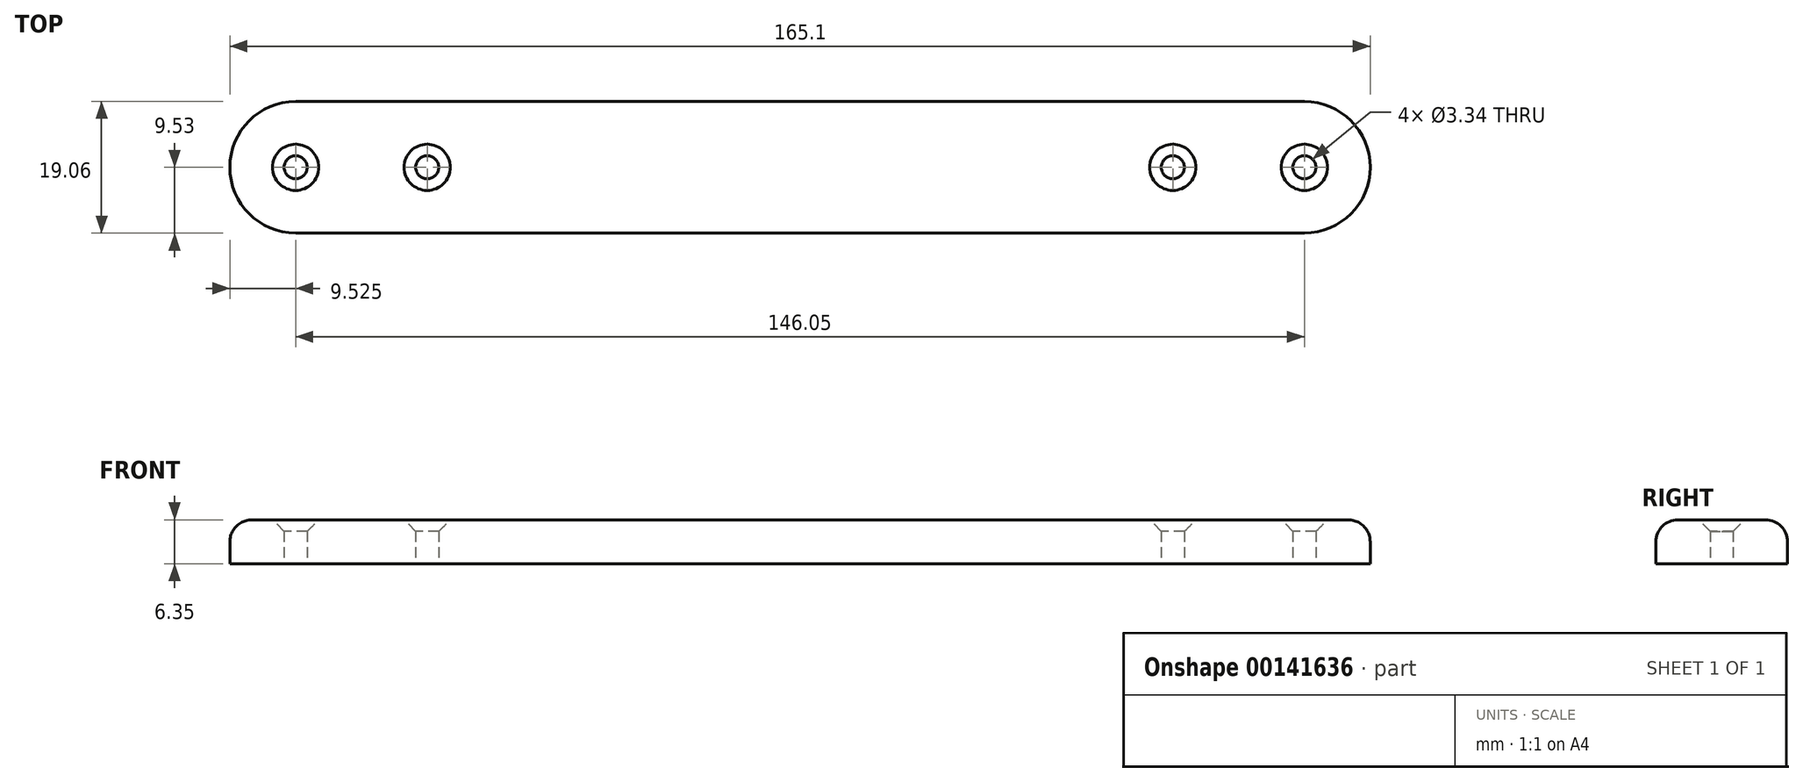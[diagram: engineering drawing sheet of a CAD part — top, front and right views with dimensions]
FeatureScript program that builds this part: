
annotation { "Feature Type Name" : "Feature", "Feature Type Description" : "" }
export const myFeature = defineFeature(function(context is Context, id is Id, definition is map)
    precondition{}
    {
        {
            var Q0;
            Q0=qCreatedBy(makeId("Top.planeOp"),FACE);
            var sketch = newSketch(context, id + "F0", { "sketchPlane" : qUnion([Q0])});
            skLineSegment(sketch, "E0.bottom", {"start": v(63.5, 9.53) * mm, "end": v(-63.5, 9.53) * mm});
            skLineSegment(sketch, "E0.top", {"start": v(63.5, -9.53) * mm, "end": v(-63.5, -9.53) * mm});
            skLineSegment(sketch, "E0.left", {"start": v(63.5, 9.53) * mm, "end": v(63.5, -9.53) * mm, "construction": true});
            skLineSegment(sketch, "E0.right", {"start": v(-63.5, 9.53) * mm, "end": v(-63.5, -9.53) * mm, "construction": true});
            skPoint(sketch, "E0.middle", {"position": v(0, 0) * mm});
            skLineSegment(sketch, "E1.bottom", {"start": v(-63.5, 9.53) * mm, "end": v(-73.02, 9.53) * mm});
            skLineSegment(sketch, "E1.top", {"start": v(-63.5, -9.53) * mm, "end": v(-73.02, -9.53) * mm});
            skLineSegment(sketch, "E1.right", {"start": v(-82.55, 0) * mm, "end": v(-82.55, 0) * mm});
            skLineSegment(sketch, "E2.bottom", {"start": v(63.5, 9.53) * mm, "end": v(73.02, 9.53) * mm});
            skLineSegment(sketch, "E2.top", {"start": v(63.5, -9.53) * mm, "end": v(73.02, -9.53) * mm});
            skLineSegment(sketch, "E2.right", {"start": v(82.55, 0) * mm, "end": v(82.55, 0) * mm});
            skLineSegment(sketch, "E3", {"start": v(0, 9.53) * mm, "end": v(0, -9.53) * mm, "construction": true});
            skCircle(sketch, "E4", {"center": v(-73.02, 0) * mm, "radius": 1.67 * mm});
            skCircle(sketch, "E5", {"center": v(-53.98, 0) * mm, "radius": 1.67 * mm});
            skCircle(sketch, "E6", {"center": v(53.98, 0) * mm, "radius": 1.67 * mm});
            skCircle(sketch, "E7", {"center": v(73.02, 0) * mm, "radius": 1.67 * mm});
            skPoint(sketch, "E8.visualSharp", {"position": v(-82.55, 9.53) * mm});
            skArc(sketch, "E8.filletArc", {"start": v(-73.02, 9.53) * mm, "mid": v(-79.76, 6.74) * mm, "end": v(-82.55, 0) * mm});
            skPoint(sketch, "E9.visualSharp", {"position": v(-82.55, -9.53) * mm});
            skArc(sketch, "E9.filletArc", {"start": v(-82.55, 0) * mm, "mid": v(-79.76, -6.74) * mm, "end": v(-73.02, -9.53) * mm});
            skPoint(sketch, "E10.visualSharp", {"position": v(82.55, 9.53) * mm});
            skArc(sketch, "E10.filletArc", {"start": v(82.55, 0) * mm, "mid": v(79.76, 6.74) * mm, "end": v(73.02, 9.53) * mm});
            skPoint(sketch, "E11.visualSharp", {"position": v(82.55, -9.53) * mm});
            skArc(sketch, "E11.filletArc", {"start": v(73.02, -9.53) * mm, "mid": v(79.76, -6.74) * mm, "end": v(82.55, 0) * mm});
            skSolve(sketch);
        }
        {
            var Q0;
            Q0=makeQuery(id+"F0.imprint","IMPRINT",FACE,{"disambiguationData":[TD([[makeQuery(id+"F0.imprint","IMPRINT",EDGE,{"derivedFrom":sQuery(id+"F0.wireOp",EDGE,"E0.bottom")}),1.0]])]});
            extrude(context, id + "F1", {"entities" : qUnion([Q0]), "depth" : 6.35 * mm});
        }
        {
            var Q0;
            Q0=makeQuery(id+"F1.opExtrude","CAP_EDGE",EDGE,{"disambiguationData":[OSD([sQuery(id+"F0.wireOp",EDGE,"E8.filletArc"),sQuery(id+"F0.wireOp",EDGE,"E9.filletArc")])],"isStart":false});
            fillet(context, id + "F2", {"entities" : qUnion([Q0]), "radius" : 3.17 * mm, "tangentPropagation" : true, "allowEdgeOverflow" : false});
        }
        {
            var Q0;
            Q0=makeQuery(id+"F1.opExtrude","CAP_EDGE",EDGE,{"disambiguationData":[OSD([sQuery(id+"F0.wireOp",EDGE,"E4")])],"isStart":false});
            var Q1;
            Q1=makeQuery(id+"F1.opExtrude","CAP_EDGE",EDGE,{"disambiguationData":[OSD([sQuery(id+"F0.wireOp",EDGE,"E5")])],"isStart":false});
            var Q2;
            Q2=makeQuery(id+"F1.opExtrude","CAP_EDGE",EDGE,{"disambiguationData":[OSD([sQuery(id+"F0.wireOp",EDGE,"E6")])],"isStart":false});
            var Q3;
            Q3=makeQuery(id+"F1.opExtrude","CAP_EDGE",EDGE,{"disambiguationData":[OSD([sQuery(id+"F0.wireOp",EDGE,"E7")])],"isStart":false});
            chamfer(context, id + "F3", {"entities" : qUnion([Q0, Q1, Q2, Q3]), "width" : 1.68 * mm, "tangentPropagation" : true});
        }
    });
